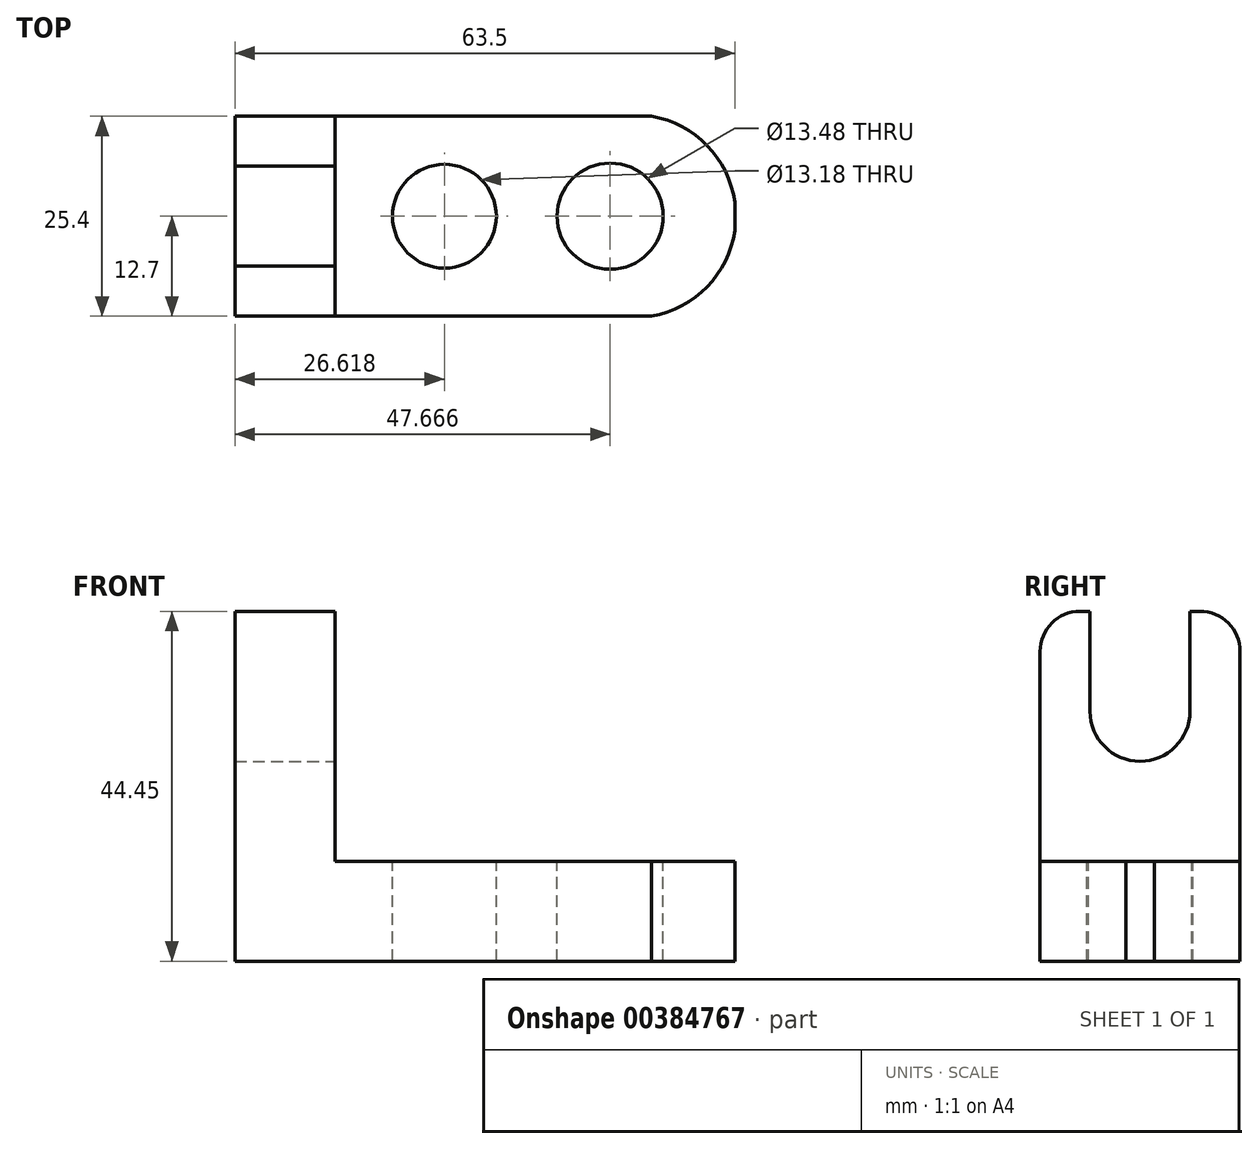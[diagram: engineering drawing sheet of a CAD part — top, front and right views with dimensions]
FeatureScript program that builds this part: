
annotation { "Feature Type Name" : "Feature", "Feature Type Description" : "" }
export const myFeature = defineFeature(function(context is Context, id is Id, definition is map)
    precondition{}
    {
        {
            var Q0;
            Q0=qCreatedBy(makeId("Front.planeOp"),FACE);
            var sketch = newSketch(context, id + "F0", { "sketchPlane" : qUnion([Q0])});
            skLineSegment(sketch, "E0", {"start": v(0, 44.45) * mm, "end": v(0, 0) * mm});
            skLineSegment(sketch, "E1", {"start": v(0, 0) * mm, "end": v(63.5, 0) * mm});
            skLineSegment(sketch, "E2", {"start": v(63.5, 0) * mm, "end": v(63.5, 12.7) * mm});
            skLineSegment(sketch, "E3", {"start": v(63.5, 12.7) * mm, "end": v(12.7, 12.7) * mm});
            skLineSegment(sketch, "E4", {"start": v(12.7, 12.7) * mm, "end": v(12.7, 44.45) * mm});
            skLineSegment(sketch, "E5", {"start": v(12.7, 44.45) * mm, "end": v(0, 44.45) * mm});
            skSolve(sketch);
        }
        {
            var Q0;
            Q0=makeQuery(id+"F0.imprint","IMPRINT",FACE,{"disambiguationData":[TD([[makeQuery(id+"F0.imprint","IMPRINT",EDGE,{"derivedFrom":sQuery(id+"F0.wireOp",EDGE,"E0")}),1.0]])]});
            extrude(context, id + "F1", {"entities" : qUnion([Q0]), "depth" : 25.4 * mm});
        }
        {
            var Q0;
            Q0=makeQuery(id+"F1.opExtrude","SWEPT_FACE",FACE,{"disambiguationData":[OSD([sQuery(id+"F0.wireOp",EDGE,"E3")])]});
            var sketch = newSketch(context, id + "F2", { "sketchPlane" : qUnion([Q0])});
            skArc(sketch, "E6", {"start": v(52.93, -25.4) * mm, "mid": v(63.63, -12.7) * mm, "end": v(52.93, 0) * mm});
            skSolve(sketch);
        }
        {
            var Q0;
            {var subQ0=sQuery(id+"F2.wireOp",EDGE,"E6");var subQ1=sQuery(id+"F0.wireOp",EDGE,"E3");var subQ2=makeQuery(id+"F1.opExtrude","CAP_EDGE",EDGE,{"disambiguationData":[OSD([subQ1])],"isStart":false});var subQ3=makeQuery(id+"F2.imprint","INTERSECT",VERTEX,{"derivedFrom":[subQ2,subQ0]});Q0=makeQuery(id+"F2.imprint","IMPRINT",FACE,{"disambiguationData":[TD([[makeQuery(id+"F2.imprint","IMPRINT",EDGE,{"disambiguationData":[TD([[subQ3,-1.0]])],"derivedFrom":subQ0}),-1.0]])]});}
            var Q1;
            {var subQ0=sQuery(id+"F2.wireOp",EDGE,"E6");var subQ1=sQuery(id+"F0.wireOp",EDGE,"E3");var subQ2=makeQuery(id+"F1.opExtrude","CAP_EDGE",EDGE,{"disambiguationData":[OSD([subQ1])],"isStart":true});var subQ3=makeQuery(id+"F2.imprint","INTERSECT",VERTEX,{"derivedFrom":[subQ2,subQ0]});Q1=makeQuery(id+"F2.imprint","IMPRINT",FACE,{"disambiguationData":[TD([[makeQuery(id+"F2.imprint","IMPRINT",EDGE,{"disambiguationData":[TD([[subQ3,1.0]])],"derivedFrom":subQ0}),-1.0]])]});}
            extrude(context, id + "F3", {"entities" : qUnion([Q0, Q1]), "operationType" : NewBodyOperationType.REMOVE, "oppositeDirection" : true, "depth" : 25.4 * mm});
        }
        {
            var Q0;
            Q0=makeQuery(id+"F1.opExtrude","SWEPT_FACE",FACE,{"disambiguationData":[OSD([sQuery(id+"F0.wireOp",EDGE,"E3")])]});
            var sketch = newSketch(context, id + "F4", { "sketchPlane" : qUnion([Q0])});
            skCircle(sketch, "E7", {"center": v(26.62, -12.7) * mm, "radius": 6.6 * mm});
            skPoint(sketch, "E7.centerSnap0", {"position": v(12.7, -12.7) * mm});
            skCircle(sketch, "E8", {"center": v(47.67, -12.7) * mm, "radius": 6.74 * mm});
            skSolve(sketch);
        }
        {
            var Q0;
            Q0 = qSketchRegion(id + "F4", true);
            extrude(context, id + "F5", {"entities" : qUnion([Q0]), "operationType" : NewBodyOperationType.REMOVE, "oppositeDirection" : true, "depth" : 25.4 * mm});
        }
        {
            var Q0;
            Q0=makeQuery(id+"F1.opExtrude","SWEPT_FACE",FACE,{"disambiguationData":[OSD([sQuery(id+"F0.wireOp",EDGE,"E4")])]});
            var sketch = newSketch(context, id + "F6", { "sketchPlane" : qUnion([Q0])});
            skLineSegment(sketch, "E9", {"start": v(-6.35, 31.75) * mm, "end": v(-6.35, 44.45) * mm});
            skLineSegment(sketch, "E10", {"start": v(-6.35, 44.45) * mm, "end": v(-19.05, 44.45) * mm});
            skLineSegment(sketch, "E11", {"start": v(-19.05, 44.45) * mm, "end": v(-19.05, 31.75) * mm});
            skArc(sketch, "E12", {"start": v(-19.05, 31.75) * mm, "mid": v(-12.7, 25.4) * mm, "end": v(-6.35, 31.75) * mm});
            skSolve(sketch);
        }
        {
            var Q0;
            Q0=makeQuery(id+"F6.imprint","IMPRINT",FACE,{"disambiguationData":[TD([[makeQuery(id+"F6.imprint","IMPRINT",EDGE,{"derivedFrom":sQuery(id+"F6.wireOp",EDGE,"E9")}),1.0]])]});
            extrude(context, id + "F7", {"entities" : qUnion([Q0]), "operationType" : NewBodyOperationType.REMOVE, "oppositeDirection" : true, "depth" : 25.4 * mm});
        }
        {
            var Q0;
            Q0=makeQuery(id+"F1.opExtrude","CAP_EDGE",EDGE,{"disambiguationData":[OSD([sQuery(id+"F0.wireOp",EDGE,"E5")])],"isStart":false});
            fillet(context, id + "F8", {"entities" : qUnion([Q0]), "radius" : 5.08 * mm, "tangentPropagation" : true, "allowEdgeOverflow" : false});
        }
        {
            var Q0;
            Q0=makeQuery(id+"F1.opExtrude","CAP_EDGE",EDGE,{"disambiguationData":[OSD([sQuery(id+"F0.wireOp",EDGE,"E5")])],"isStart":true});
            fillet(context, id + "F9", {"entities" : qUnion([Q0]), "radius" : 5.08 * mm, "tangentPropagation" : true, "allowEdgeOverflow" : false});
        }
    });
